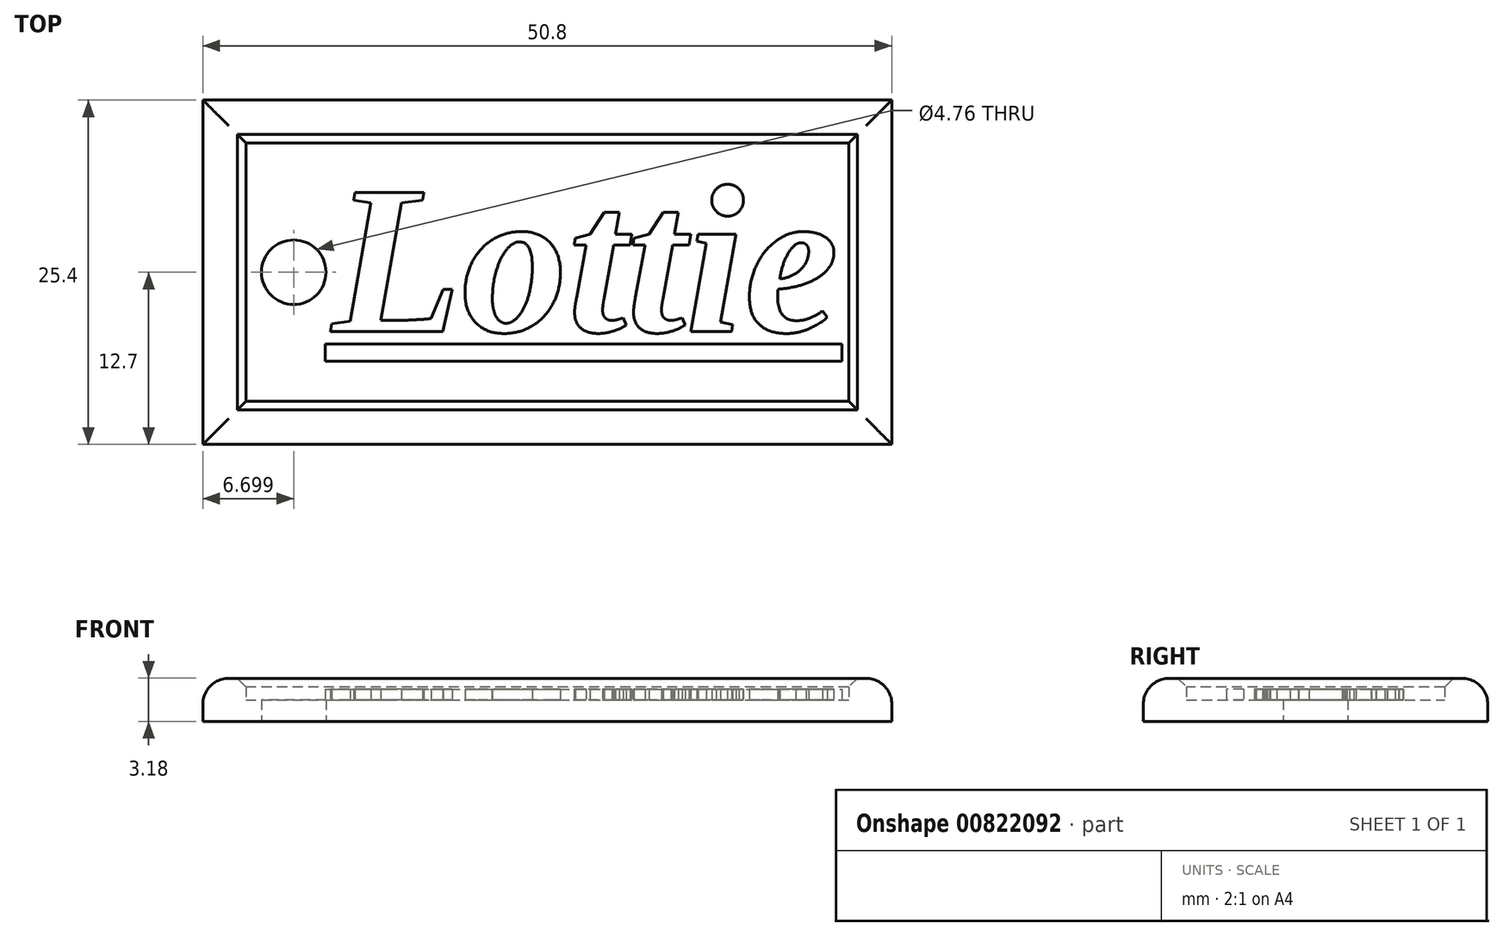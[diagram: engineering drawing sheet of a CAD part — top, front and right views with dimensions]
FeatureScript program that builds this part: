
annotation { "Feature Type Name" : "Feature", "Feature Type Description" : "" }
export const myFeature = defineFeature(function(context is Context, id is Id, definition is map)
    precondition{}
    {
        {
            var Q0;
            Q0=qCreatedBy(makeId("Top.planeOp"),FACE);
            var sketch = newSketch(context, id + "F0", { "sketchPlane" : qUnion([Q0])});
            skLineSegment(sketch, "E0.bottom", {"start": v(0, 0) * mm, "end": v(50.8, 0) * mm});
            skLineSegment(sketch, "E0.top", {"start": v(0, 25.4) * mm, "end": v(50.8, 25.4) * mm});
            skLineSegment(sketch, "E0.left", {"start": v(0, 0) * mm, "end": v(0, 25.4) * mm});
            skLineSegment(sketch, "E0.right", {"start": v(50.8, 0) * mm, "end": v(50.8, 25.4) * mm});
            skLineSegment(sketch, "E1.0", {"start": v(3.17, 22.23) * mm, "end": v(47.62, 22.23) * mm});
            skLineSegment(sketch, "E1.1", {"start": v(3.18, 3.18) * mm, "end": v(3.17, 22.23) * mm});
            skLineSegment(sketch, "E1.2", {"start": v(3.18, 3.18) * mm, "end": v(47.62, 3.18) * mm});
            skLineSegment(sketch, "E1.3", {"start": v(47.62, 3.18) * mm, "end": v(47.62, 22.23) * mm});
            skCircle(sketch, "E2", {"center": v(6.7, 12.7) * mm, "radius": 2.38 * mm});
            skPoint(sketch, "E2.centerSnap0", {"position": v(3.17, 12.7) * mm});
            skSolve(sketch);
        }
        {
            var Q0;
            Q0=makeQuery(id+"F0.imprint","IMPRINT",FACE,{"disambiguationData":[TD([[makeQuery(id+"F0.imprint","IMPRINT",EDGE,{"derivedFrom":sQuery(id+"F0.wireOp",EDGE,"E1.0")}),-1.0]])]});
            extrude(context, id + "F1", {"entities" : qUnion([Q0]), "depth" : 1.59 * mm, "offsetDistance" : 25.4 * mm});
        }
        {
            var Q0;
            Q0 = qSketchRegion(id + "F0", true);
            extrude(context, id + "F2", {"entities" : qUnion([Q0]), "operationType" : NewBodyOperationType.ADD, "depth" : 3.17 * mm, "offsetDistance" : 25.4 * mm});
        }
        {
            var Q0;
            Q0=makeQuery(id+"F1.opExtrude","CAP_FACE",FACE,{"disambiguationData":[OSD([sQuery(id+"F0.wireOp",EDGE,"E1.0"),sQuery(id+"F0.wireOp",EDGE,"E1.1"),sQuery(id+"F0.wireOp",EDGE,"E1.2"),sQuery(id+"F0.wireOp",EDGE,"E1.3"),sQuery(id+"F0.wireOp",EDGE,"E2")])],"isStart":false});
            var sketch = newSketch(context, id + "F3", { "sketchPlane" : qUnion([Q0])});
            skText(sketch, "E3", { "text": "Lottie", "fontName": "Tinos-BoldItalic.ttf"});
            skLineSegment(sketch, "E4.bottom", {"start": v(9.02, 7.4) * mm, "end": v(47.12, 7.4) * mm});
            skLineSegment(sketch, "E4.top", {"start": v(9.02, 6.13) * mm, "end": v(47.12, 6.13) * mm});
            skLineSegment(sketch, "E4.left", {"start": v(9.02, 7.4) * mm, "end": v(9.02, 6.13) * mm});
            skLineSegment(sketch, "E4.right", {"start": v(47.12, 7.4) * mm, "end": v(47.12, 6.13) * mm});
            const initialGuessF3  = {"E3": [0.00953, 0.00833, 1, 0, 0.01126]};
            skSetInitialGuess(sketch, initialGuessF3);
            skSolve(sketch);
        }
        {
            var Q0;
            Q0 = qSketchRegion(id + "F3", true);
            extrude(context, id + "F4", {"entities" : qUnion([Q0]), "operationType" : NewBodyOperationType.ADD, "depth" : 0.8 * mm, "offsetDistance" : 25.4 * mm});
        }
        {
            var Q0;
            Q0=makeQuery(id+"F2.opExtrude","CAP_EDGE",EDGE,{"disambiguationData":[OSD([sQuery(id+"F0.wireOp",EDGE,"E0.bottom")])],"isStart":false});
            var Q1;
            Q1=makeQuery(id+"F2.opExtrude","CAP_EDGE",EDGE,{"disambiguationData":[OSD([sQuery(id+"F0.wireOp",EDGE,"E0.left")])],"isStart":false});
            var Q2;
            Q2=makeQuery(id+"F2.opExtrude","CAP_EDGE",EDGE,{"disambiguationData":[OSD([sQuery(id+"F0.wireOp",EDGE,"E0.top")])],"isStart":false});
            var Q3;
            Q3=makeQuery(id+"F2.opExtrude","CAP_EDGE",EDGE,{"disambiguationData":[OSD([sQuery(id+"F0.wireOp",EDGE,"E0.right")])],"isStart":false});
            fillet(context, id + "F5", {"entities" : qUnion([Q0, Q1, Q2, Q3]), "radius" : 1.9 * mm, "tangentPropagation" : true, "allowEdgeOverflow" : false});
        }
        {
            var Q0;
            Q0=makeQuery(id+"F2.opExtrude","CAP_EDGE",EDGE,{"disambiguationData":[OSD([sQuery(id+"F0.wireOp",EDGE,"E1.0")])],"isStart":false});
            var Q1;
            Q1=makeQuery(id+"F2.opExtrude","CAP_EDGE",EDGE,{"disambiguationData":[OSD([sQuery(id+"F0.wireOp",EDGE,"E1.3")])],"isStart":false});
            var Q2;
            Q2=makeQuery(id+"F2.opExtrude","CAP_EDGE",EDGE,{"disambiguationData":[OSD([sQuery(id+"F0.wireOp",EDGE,"E1.2")])],"isStart":false});
            var Q3;
            Q3=makeQuery(id+"F2.opExtrude","CAP_EDGE",EDGE,{"disambiguationData":[OSD([sQuery(id+"F0.wireOp",EDGE,"E1.1")])],"isStart":false});
            chamfer(context, id + "F6", {"entities" : qUnion([Q0, Q1, Q2, Q3]), "width" : 0.64 * mm, "tangentPropagation" : true});
        }
    });
